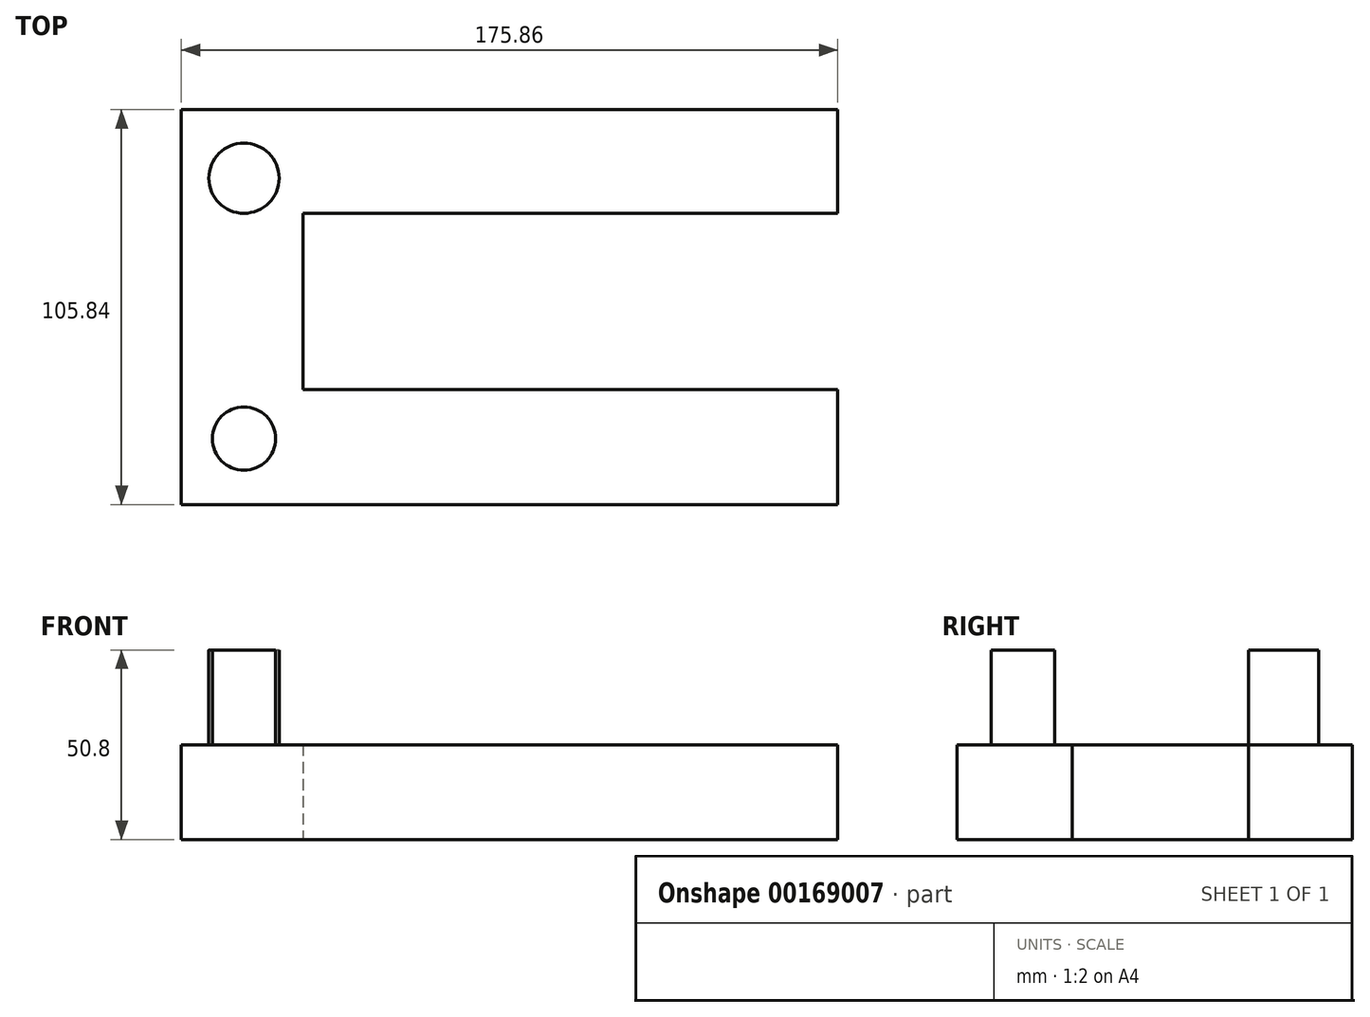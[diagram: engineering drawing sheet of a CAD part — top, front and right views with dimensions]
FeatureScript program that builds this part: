
annotation { "Feature Type Name" : "Feature", "Feature Type Description" : "" }
export const myFeature = defineFeature(function(context is Context, id is Id, definition is map)
    precondition{}
    {
        {
            var Q0;
            Q0=qCreatedBy(makeId("Top.planeOp"),FACE);
            var sketch = newSketch(context, id + "F0", { "sketchPlane" : qUnion([Q0])});
            skLineSegment(sketch, "E0", {"start": v(0, 0) * mm, "end": v(175.86, 0) * mm});
            skLineSegment(sketch, "E1", {"start": v(0, 0) * mm, "end": v(0, 105.84) * mm});
            skLineSegment(sketch, "E2", {"start": v(0, 105.84) * mm, "end": v(175.86, 105.84) * mm});
            skLineSegment(sketch, "E3", {"start": v(175.86, 105.84) * mm, "end": v(175.86, 78.06) * mm});
            skLineSegment(sketch, "E4", {"start": v(175.86, 78.06) * mm, "end": v(32.63, 78.06) * mm});
            skLineSegment(sketch, "E5", {"start": v(32.63, 78.06) * mm, "end": v(32.63, 30.87) * mm});
            skLineSegment(sketch, "E6", {"start": v(32.63, 30.87) * mm, "end": v(175.86, 30.87) * mm});
            skLineSegment(sketch, "E7", {"start": v(175.86, 30.87) * mm, "end": v(175.86, 0) * mm});
            skSolve(sketch);
        }
        {
            var Q0;
            Q0=makeQuery(id+"F0.imprint","IMPRINT",FACE,{"disambiguationData":[TD([[makeQuery(id+"F0.imprint","IMPRINT",EDGE,{"derivedFrom":sQuery(id+"F0.wireOp",EDGE,"E0")}),1.0]])]});
            extrude(context, id + "F1", {"entities" : qUnion([Q0]), "depth" : 25.4 * mm});
        }
        {
            var Q0;
            Q0=makeQuery(id+"F1.opExtrude","CAP_FACE",FACE,{"disambiguationData":[OSD([sQuery(id+"F0.wireOp",EDGE,"E0"),sQuery(id+"F0.wireOp",EDGE,"E1"),sQuery(id+"F0.wireOp",EDGE,"E2"),sQuery(id+"F0.wireOp",EDGE,"E3"),sQuery(id+"F0.wireOp",EDGE,"E4"),sQuery(id+"F0.wireOp",EDGE,"E5"),sQuery(id+"F0.wireOp",EDGE,"E6"),sQuery(id+"F0.wireOp",EDGE,"E7")])],"isStart":false});
            var sketch = newSketch(context, id + "F2", { "sketchPlane" : qUnion([Q0])});
            skCircle(sketch, "E8", {"center": v(16.76, 87.47) * mm, "radius": 9.41 * mm});
            skCircle(sketch, "E9", {"center": v(16.76, 17.66) * mm, "radius": 8.48 * mm});
            skSolve(sketch);
        }
        {
            var Q0;
            Q0 = qSketchRegion(id + "F2", true);
            extrude(context, id + "F3", {"entities" : qUnion([Q0]), "operationType" : NewBodyOperationType.ADD, "depth" : 25.4 * mm});
        }
    });
